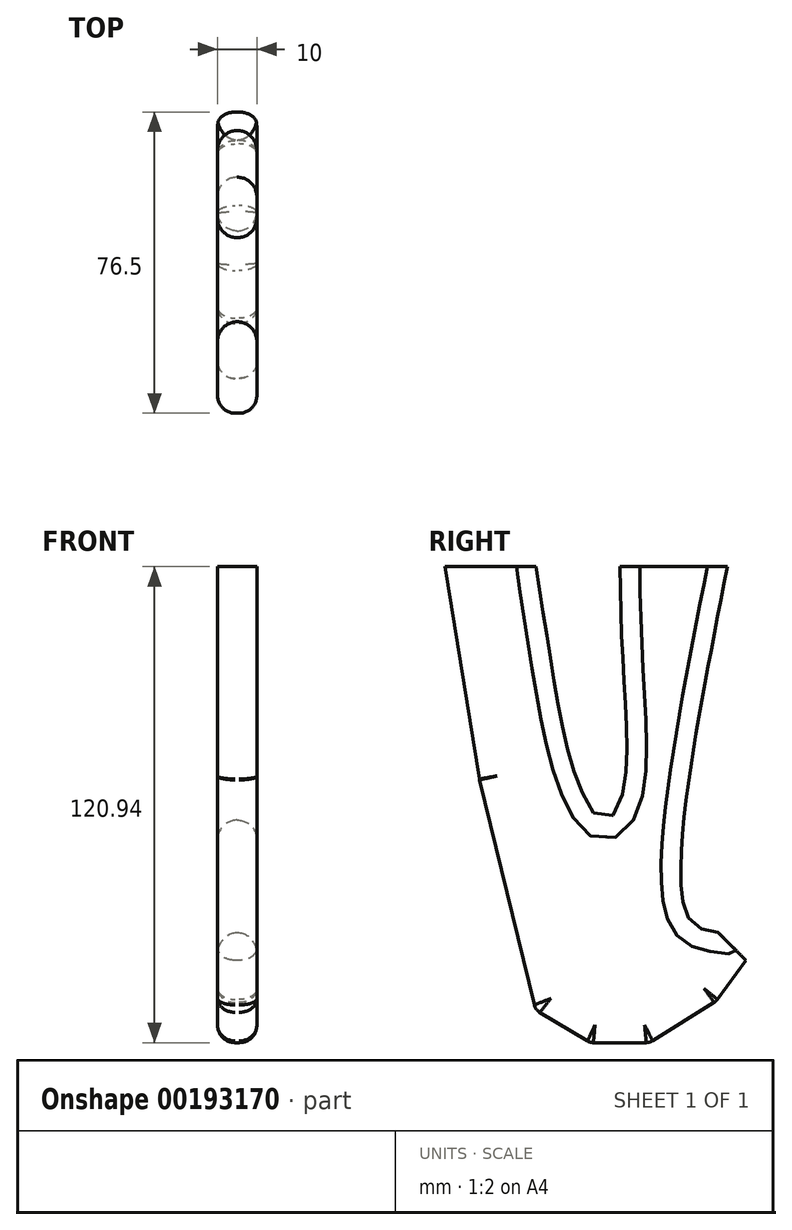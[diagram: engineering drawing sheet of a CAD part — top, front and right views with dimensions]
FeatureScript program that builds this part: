
annotation { "Feature Type Name" : "Feature", "Feature Type Description" : "" }
export const myFeature = defineFeature(function(context is Context, id is Id, definition is map)
    precondition{}
    {
        {
            var Q0;
            Q0=qCreatedBy(makeId("Top.planeOp"),FACE);
            var sketch = newSketch(context, id + "F0", { "sketchPlane" : qUnion([Q0])});
            skLineSegment(sketch, "E0.bottom", {"start": v(50, 50) * mm, "end": v(-50, 50) * mm});
            skLineSegment(sketch, "E0.top", {"start": v(50, -50) * mm, "end": v(-50, -50) * mm});
            skLineSegment(sketch, "E0.left", {"start": v(50, 50) * mm, "end": v(50, -50) * mm});
            skLineSegment(sketch, "E0.right", {"start": v(-50, 50) * mm, "end": v(-50, -50) * mm});
            skPoint(sketch, "E0.middle", {"position": v(0, 0) * mm});
            skSolve(sketch);
        }
        {
            var Q0;
            Q0=qCreatedBy(makeId("Right.planeOp"),FACE);
            var sketch = newSketch(context, id + "F1", { "sketchPlane" : qUnion([Q0])});
            skLineSegment(sketch, "E1", {"start": v(32.93, -92.93) * mm, "end": v(40, -100) * mm});
            skLineSegment(sketch, "E2", {"start": v(40, -100) * mm, "end": v(50, -100) * mm});
            skLineSegment(sketch, "E3", {"start": v(50, -100) * mm, "end": v(50, 0) * mm});
            skLineSegment(sketch, "E4", {"start": v(40, -100) * mm, "end": v(32.42, -110.44) * mm});
            skLineSegment(sketch, "E5", {"start": v(32.42, -110.44) * mm, "end": v(15.56, -120.94) * mm});
            skLineSegment(sketch, "E6", {"start": v(15.56, -120.94) * mm, "end": v(0.42, -120.94) * mm});
            skLineSegment(sketch, "E7", {"start": v(0.42, -120.94) * mm, "end": v(-13.45, -112.58) * mm});
            skLineSegment(sketch, "E8", {"start": v(-13.45, -112.58) * mm, "end": v(-27.68, -54.06) * mm});
            skLineSegment(sketch, "E9", {"start": v(-27.68, -54.06) * mm, "end": v(-36.5, 0) * mm});
            skFitSpline(sketch, "E10", {"points": [v(32.93, -92.93) * mm, v(25.29, -88.96) * mm, v(35.31, 0) * mm], "startDerivative": vector(-37.65, 4.94) * mm, "endDerivative": vector(30.46, 154.64) * mm});
            skFitSpline(sketch, "E11", {"points": [v(8.07, 0) * mm, v(8.9, -56.9) * mm, v(4.16, -64.38) * mm, v(-2.6, -54.96) * mm, v(-13.28, 0) * mm], "startDerivative": vector(0.01, -244.79) * mm, "endDerivative": vector(-35.2, 225.8) * mm});
            skLineSegment(sketch, "E12", {"start": v(35.31, 0) * mm, "end": v(8.07, 0) * mm});
            skLineSegment(sketch, "E13", {"start": v(-13.28, 0) * mm, "end": v(-36.5, 0) * mm});
            skSolve(sketch);
        }
        {
            var Q0;
            Q0=sQuery(id+"F1.wireOp",EDGE,"E1");
            extrude(context, id + "F2", {"bodyType" : ToolBodyType.SURFACE, "surfaceEntities" : qUnion([Q0]), "endBound" : BoundingType.SYMMETRIC, "depth" : 10 * mm});
        }
        {
            var Q0;
            Q0 = qSketchRegion(id + "F1", true);
            extrude(context, id + "F3", {"entities" : qUnion([Q0]), "endBound" : BoundingType.SYMMETRIC, "depth" : 10 * mm});
        }
        {
            var Q0;
            Q0=makeQuery(id+"F3.opExtrude","CAP_EDGE",EDGE,{"disambiguationData":[OSD([sQuery(id+"F1.wireOp",EDGE,"6j2MmI0v-9CaA-rXXN-4GS7-BZTnkRh6syKU")])],"isStart":false});
            var Q1;
            Q1=makeQuery(id+"F3.opExtrude","CAP_EDGE",EDGE,{"disambiguationData":[OSD([sQuery(id+"F1.wireOp",EDGE,"E4")])],"isStart":false});
            var Q2;
            Q2=makeQuery(id+"F3.opExtrude","CAP_EDGE",EDGE,{"disambiguationData":[OSD([sQuery(id+"F1.wireOp",EDGE,"E4")])],"isStart":true});
            var Q3;
            Q3=makeQuery(id+"F3.opExtrude","CAP_EDGE",EDGE,{"disambiguationData":[OSD([sQuery(id+"F1.wireOp",EDGE,"6j2MmI0v-9CaA-rXXN-4GS7-BZTnkRh6syKU")])],"isStart":true});
            var Q4;
            Q4=makeQuery(id+"F3.opExtrude","CAP_EDGE",EDGE,{"disambiguationData":[OSD([sQuery(id+"F1.wireOp",EDGE,"1lMwgCfK-8zYP-9geR-T3N1-000Z4BXpfQfB")])],"isStart":false});
            var Q5;
            Q5=makeQuery(id+"F3.opExtrude","CAP_EDGE",EDGE,{"disambiguationData":[OSD([sQuery(id+"F1.wireOp",EDGE,"1lMwgCfK-8zYP-9geR-T3N1-000Z4BXpfQfB")])],"isStart":true});
            var Q6;
            Q6=makeQuery(id+"F3.opExtrude","CAP_EDGE",EDGE,{"disambiguationData":[OSD([sQuery(id+"F1.wireOp",EDGE,"E5")])],"isStart":false});
            var Q7;
            Q7=makeQuery(id+"F3.opExtrude","CAP_EDGE",EDGE,{"disambiguationData":[OSD([sQuery(id+"F1.wireOp",EDGE,"E5")])],"isStart":true});
            var Q8;
            Q8=makeQuery(id+"F3.opExtrude","CAP_EDGE",EDGE,{"disambiguationData":[OSD([sQuery(id+"F1.wireOp",EDGE,"E6")])],"isStart":true});
            var Q9;
            Q9=makeQuery(id+"F3.opExtrude","CAP_EDGE",EDGE,{"disambiguationData":[OSD([sQuery(id+"F1.wireOp",EDGE,"E6")])],"isStart":false});
            var Q10;
            Q10=makeQuery(id+"F3.opExtrude","CAP_EDGE",EDGE,{"disambiguationData":[OSD([sQuery(id+"F1.wireOp",EDGE,"E7")])],"isStart":false});
            var Q11;
            Q11=makeQuery(id+"F3.opExtrude","CAP_EDGE",EDGE,{"disambiguationData":[OSD([sQuery(id+"F1.wireOp",EDGE,"E7")])],"isStart":true});
            var Q12;
            Q12=makeQuery(id+"F3.opExtrude","CAP_EDGE",EDGE,{"disambiguationData":[OSD([sQuery(id+"F1.wireOp",EDGE,"E8")])],"isStart":true});
            var Q13;
            Q13=makeQuery(id+"F3.opExtrude","CAP_EDGE",EDGE,{"disambiguationData":[OSD([sQuery(id+"F1.wireOp",EDGE,"E9")])],"isStart":true});
            var Q14;
            Q14=makeQuery(id+"F3.opExtrude","CAP_EDGE",EDGE,{"disambiguationData":[OSD([sQuery(id+"F1.wireOp",EDGE,"E8")])],"isStart":false});
            var Q15;
            Q15=makeQuery(id+"F3.opExtrude","CAP_EDGE",EDGE,{"disambiguationData":[OSD([sQuery(id+"F1.wireOp",EDGE,"E9")])],"isStart":false});
            var Q16;
            Q16=makeQuery(id+"F3.opExtrude","CAP_EDGE",EDGE,{"disambiguationData":[OSD([sQuery(id+"F1.wireOp",EDGE,"PjlUZDiv-9Nuz-91em-e2Fd-0O4rsgYu6psd")])],"isStart":false});
            var Q17;
            Q17=makeQuery(id+"F3.opExtrude","CAP_EDGE",EDGE,{"disambiguationData":[OSD([sQuery(id+"F1.wireOp",EDGE,"PjlUZDiv-9Nuz-91em-e2Fd-0O4rsgYu6psd")])],"isStart":true});
            var Q18;
            Q18=makeQuery(id+"F3.opExtrude","CAP_EDGE",EDGE,{"disambiguationData":[OSD([sQuery(id+"F1.wireOp",EDGE,"ZAGma3XW-A2qp-hiio-JgDo-AlgzH9WFpZtm")])],"isStart":false});
            var Q19;
            Q19=makeQuery(id+"F3.opExtrude","CAP_EDGE",EDGE,{"disambiguationData":[OSD([sQuery(id+"F1.wireOp",EDGE,"ZAGma3XW-A2qp-hiio-JgDo-AlgzH9WFpZtm")])],"isStart":true});
            fillet(context, id + "F4", {"entities" : qUnion([Q0, Q1, Q2, Q3, Q4, Q5, Q6, Q7, Q8, Q9, Q10, Q11, Q12, Q13, Q14, Q15, Q16, Q17, Q18, Q19]), "radius" : 4.5 * mm, "tangentPropagation" : true, "allowEdgeOverflow" : false});
        }
        {
            var Q0;
            Q0=makeQuery(id+"F4.opFillet","BLEND_EDGE",EDGE,{"blendedFrom":[makeQuery(id+"F3.opExtrude","CAP_EDGE",EDGE,{"disambiguationData":[OSD([sQuery(id+"F1.wireOp",EDGE,"1lMwgCfK-8zYP-9geR-T3N1-000Z4BXpfQfB")])],"isStart":false}),makeQuery(id+"F3.opExtrude","CAP_EDGE",EDGE,{"disambiguationData":[OSD([sQuery(id+"F1.wireOp",EDGE,"PjlUZDiv-9Nuz-91em-e2Fd-0O4rsgYu6psd")])],"isStart":false})],"blendedInto":[]});
            var Q1;
            Q1=makeQuery(id+"F4.opFillet","BLEND_EDGE",EDGE,{"blendedFrom":[makeQuery(id+"F3.opExtrude","CAP_EDGE",EDGE,{"disambiguationData":[OSD([sQuery(id+"F1.wireOp",EDGE,"1lMwgCfK-8zYP-9geR-T3N1-000Z4BXpfQfB")])],"isStart":true}),makeQuery(id+"F3.opExtrude","CAP_EDGE",EDGE,{"disambiguationData":[OSD([sQuery(id+"F1.wireOp",EDGE,"PjlUZDiv-9Nuz-91em-e2Fd-0O4rsgYu6psd")])],"isStart":true})],"blendedInto":[]});
            var Q2;
            Q2=makeQuery(id+"F4.opFillet","BLEND_EDGE",EDGE,{"blendedFrom":[makeQuery(id+"F3.opExtrude","CAP_EDGE",EDGE,{"disambiguationData":[OSD([sQuery(id+"F1.wireOp",EDGE,"6j2MmI0v-9CaA-rXXN-4GS7-BZTnkRh6syKU")])],"isStart":false}),makeQuery(id+"F3.opExtrude","CAP_EDGE",EDGE,{"disambiguationData":[OSD([sQuery(id+"F1.wireOp",EDGE,"1lMwgCfK-8zYP-9geR-T3N1-000Z4BXpfQfB")])],"isStart":false})],"blendedInto":[]});
            var Q3;
            Q3=makeQuery(id+"F4.opFillet","BLEND_EDGE",EDGE,{"blendedFrom":[makeQuery(id+"F3.opExtrude","CAP_EDGE",EDGE,{"disambiguationData":[OSD([sQuery(id+"F1.wireOp",EDGE,"6j2MmI0v-9CaA-rXXN-4GS7-BZTnkRh6syKU")])],"isStart":true}),makeQuery(id+"F3.opExtrude","CAP_EDGE",EDGE,{"disambiguationData":[OSD([sQuery(id+"F1.wireOp",EDGE,"1lMwgCfK-8zYP-9geR-T3N1-000Z4BXpfQfB")])],"isStart":true})],"blendedInto":[]});
            var Q4;
            Q4=makeQuery(id+"F4.opFillet","BLEND_EDGE",EDGE,{"blendedFrom":[makeQuery(id+"F3.opExtrude","CAP_EDGE",EDGE,{"disambiguationData":[OSD([sQuery(id+"F1.wireOp",EDGE,"PjlUZDiv-9Nuz-91em-e2Fd-0O4rsgYu6psd")])],"isStart":false}),makeQuery(id+"F3.opExtrude","CAP_EDGE",EDGE,{"disambiguationData":[OSD([sQuery(id+"F1.wireOp",EDGE,"ZAGma3XW-A2qp-hiio-JgDo-AlgzH9WFpZtm")])],"isStart":false})],"blendedInto":[]});
            var Q5;
            Q5=makeQuery(id+"F4.opFillet","BLEND_EDGE",EDGE,{"blendedFrom":[makeQuery(id+"F3.opExtrude","CAP_EDGE",EDGE,{"disambiguationData":[OSD([sQuery(id+"F1.wireOp",EDGE,"PjlUZDiv-9Nuz-91em-e2Fd-0O4rsgYu6psd")])],"isStart":true}),makeQuery(id+"F3.opExtrude","CAP_EDGE",EDGE,{"disambiguationData":[OSD([sQuery(id+"F1.wireOp",EDGE,"ZAGma3XW-A2qp-hiio-JgDo-AlgzH9WFpZtm")])],"isStart":true})],"blendedInto":[]});
            var Q6;
            Q6=makeQuery(id+"F4.opFillet","BLEND_EDGE",EDGE,{"blendedFrom":[makeQuery(id+"F3.opExtrude","CAP_EDGE",EDGE,{"disambiguationData":[OSD([sQuery(id+"F1.wireOp",EDGE,"E4")])],"isStart":true}),makeQuery(id+"F3.opExtrude","CAP_EDGE",EDGE,{"disambiguationData":[OSD([sQuery(id+"F1.wireOp",EDGE,"E5")])],"isStart":true})],"blendedInto":[]});
            var Q7;
            Q7=makeQuery(id+"F4.opFillet","BLEND_EDGE",EDGE,{"blendedFrom":[makeQuery(id+"F3.opExtrude","CAP_EDGE",EDGE,{"disambiguationData":[OSD([sQuery(id+"F1.wireOp",EDGE,"E4")])],"isStart":false}),makeQuery(id+"F3.opExtrude","CAP_EDGE",EDGE,{"disambiguationData":[OSD([sQuery(id+"F1.wireOp",EDGE,"E5")])],"isStart":false})],"blendedInto":[]});
            var Q8;
            Q8=makeQuery(id+"F4.opFillet","BLEND_EDGE",EDGE,{"blendedFrom":[makeQuery(id+"F3.opExtrude","CAP_EDGE",EDGE,{"disambiguationData":[OSD([sQuery(id+"F1.wireOp",EDGE,"E5")])],"isStart":true}),makeQuery(id+"F3.opExtrude","CAP_EDGE",EDGE,{"disambiguationData":[OSD([sQuery(id+"F1.wireOp",EDGE,"E6")])],"isStart":true})],"blendedInto":[]});
            var Q9;
            Q9=makeQuery(id+"F4.opFillet","BLEND_EDGE",EDGE,{"blendedFrom":[makeQuery(id+"F3.opExtrude","CAP_EDGE",EDGE,{"disambiguationData":[OSD([sQuery(id+"F1.wireOp",EDGE,"E5")])],"isStart":false}),makeQuery(id+"F3.opExtrude","CAP_EDGE",EDGE,{"disambiguationData":[OSD([sQuery(id+"F1.wireOp",EDGE,"E6")])],"isStart":false})],"blendedInto":[]});
            var Q10;
            Q10=makeQuery(id+"F4.opFillet","BLEND_EDGE",EDGE,{"blendedFrom":[makeQuery(id+"F3.opExtrude","CAP_EDGE",EDGE,{"disambiguationData":[OSD([sQuery(id+"F1.wireOp",EDGE,"E6")])],"isStart":false}),makeQuery(id+"F3.opExtrude","CAP_EDGE",EDGE,{"disambiguationData":[OSD([sQuery(id+"F1.wireOp",EDGE,"E7")])],"isStart":false})],"blendedInto":[]});
            var Q11;
            Q11=makeQuery(id+"F4.opFillet","BLEND_EDGE",EDGE,{"blendedFrom":[makeQuery(id+"F3.opExtrude","CAP_EDGE",EDGE,{"disambiguationData":[OSD([sQuery(id+"F1.wireOp",EDGE,"E6")])],"isStart":true}),makeQuery(id+"F3.opExtrude","CAP_EDGE",EDGE,{"disambiguationData":[OSD([sQuery(id+"F1.wireOp",EDGE,"E7")])],"isStart":true})],"blendedInto":[]});
            var Q12;
            Q12=makeQuery(id+"F4.opFillet","BLEND_EDGE",EDGE,{"blendedFrom":[makeQuery(id+"F3.opExtrude","CAP_EDGE",EDGE,{"disambiguationData":[OSD([sQuery(id+"F1.wireOp",EDGE,"E7")])],"isStart":true}),makeQuery(id+"F3.opExtrude","CAP_EDGE",EDGE,{"disambiguationData":[OSD([sQuery(id+"F1.wireOp",EDGE,"E8")])],"isStart":true})],"blendedInto":[]});
            var Q13;
            Q13=makeQuery(id+"F4.opFillet","BLEND_EDGE",EDGE,{"blendedFrom":[makeQuery(id+"F3.opExtrude","CAP_EDGE",EDGE,{"disambiguationData":[OSD([sQuery(id+"F1.wireOp",EDGE,"E7")])],"isStart":false}),makeQuery(id+"F3.opExtrude","CAP_EDGE",EDGE,{"disambiguationData":[OSD([sQuery(id+"F1.wireOp",EDGE,"E8")])],"isStart":false})],"blendedInto":[]});
            var Q14;
            Q14=makeQuery(id+"F4.opFillet","BLEND_EDGE",EDGE,{"blendedFrom":[makeQuery(id+"F3.opExtrude","CAP_EDGE",EDGE,{"disambiguationData":[OSD([sQuery(id+"F1.wireOp",EDGE,"E8")])],"isStart":true}),makeQuery(id+"F3.opExtrude","CAP_EDGE",EDGE,{"disambiguationData":[OSD([sQuery(id+"F1.wireOp",EDGE,"E9")])],"isStart":true})],"blendedInto":[]});
            var Q15;
            Q15=makeQuery(id+"F4.opFillet","BLEND_EDGE",EDGE,{"blendedFrom":[makeQuery(id+"F3.opExtrude","CAP_EDGE",EDGE,{"disambiguationData":[OSD([sQuery(id+"F1.wireOp",EDGE,"E8")])],"isStart":false}),makeQuery(id+"F3.opExtrude","CAP_EDGE",EDGE,{"disambiguationData":[OSD([sQuery(id+"F1.wireOp",EDGE,"E9")])],"isStart":false})],"blendedInto":[]});
            fillet(context, id + "F5", {"entities" : qUnion([Q0, Q1, Q2, Q3, Q4, Q5, Q6, Q7, Q8, Q9, Q10, Q11, Q12, Q13, Q14, Q15]), "radius" : 3 * mm, "tangentPropagation" : true, "allowEdgeOverflow" : false});
        }
        {
            var Q0;
            Q0=makeQuery(id+"F3.opExtrude","CAP_EDGE",EDGE,{"disambiguationData":[OSD([sQuery(id+"F1.wireOp",EDGE,"E10")])],"isStart":false});
            var Q1;
            Q1=makeQuery(id+"F3.opExtrude","CAP_EDGE",EDGE,{"disambiguationData":[OSD([sQuery(id+"F1.wireOp",EDGE,"E10")])],"isStart":true});
            var Q2;
            Q2=makeQuery(id+"F3.opExtrude","CAP_EDGE",EDGE,{"disambiguationData":[OSD([sQuery(id+"F1.wireOp",EDGE,"E11")])],"isStart":false});
            var Q3;
            Q3=makeQuery(id+"F3.opExtrude","CAP_EDGE",EDGE,{"disambiguationData":[OSD([sQuery(id+"F1.wireOp",EDGE,"E11")])],"isStart":true});
            fillet(context, id + "F6", {"entities" : qUnion([Q0, Q1, Q2, Q3]), "radius" : 5 * mm, "tangentPropagation" : true, "allowEdgeOverflow" : false});
        }
    });
